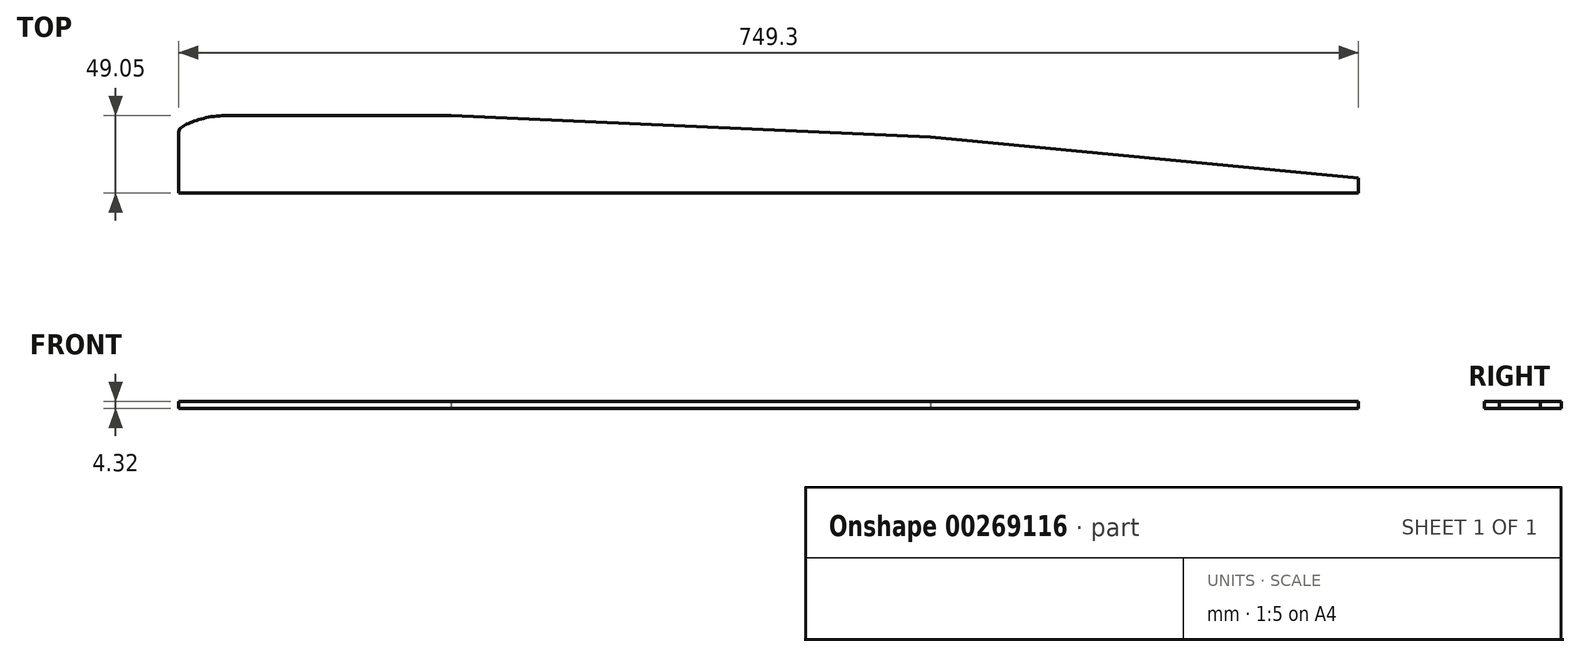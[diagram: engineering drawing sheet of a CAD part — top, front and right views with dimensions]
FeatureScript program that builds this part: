
annotation { "Feature Type Name" : "Feature", "Feature Type Description" : "" }
export const myFeature = defineFeature(function(context is Context, id is Id, definition is map)
    precondition{}
    {
        {
            var Q0;
            Q0=qCreatedBy(makeId("Top.planeOp"),FACE);
            var sketch = newSketch(context, id + "F0", { "sketchPlane" : qUnion([Q0])});
            skLineSegment(sketch, "E0", {"start": v(0, 38.74) * mm, "end": v(0, 0) * mm});
            skLineSegment(sketch, "E1", {"start": v(0, 0) * mm, "end": v(749.3, 0) * mm});
            skLineSegment(sketch, "E2", {"start": v(749.3, 0) * mm, "end": v(749.3, 9.52) * mm});
            skLineSegment(sketch, "E3", {"start": v(749.3, 9.52) * mm, "end": v(477.41, 35.56) * mm});
            skLineSegment(sketch, "E4", {"start": v(477.41, 35.56) * mm, "end": v(172.91, 49.05) * mm});
            skLineSegment(sketch, "E5", {"start": v(172.91, 49.05) * mm, "end": v(29.5, 49.05) * mm});
            skFitSpline(sketch, "E6", {"points": [v(0, 38.74) * mm, v(3.66, 42.83) * mm, v(13.13, 46.64) * mm, v(29.5, 49.05) * mm], "startDerivative": vector(0, 25.08) * mm, "endDerivative": vector(41.17, 0) * mm});
            skPoint(sketch, "E7.orphan", {"position": v(0, -38.74) * mm});
            skSolve(sketch);
        }
        {
            var Q0;
            Q0=qSketchRegion(id+"F0",true);
            extrude(context, id + "F1", {"entities" : qUnion([Q0]), "depth" : 4.32 * mm});
        }
    });
